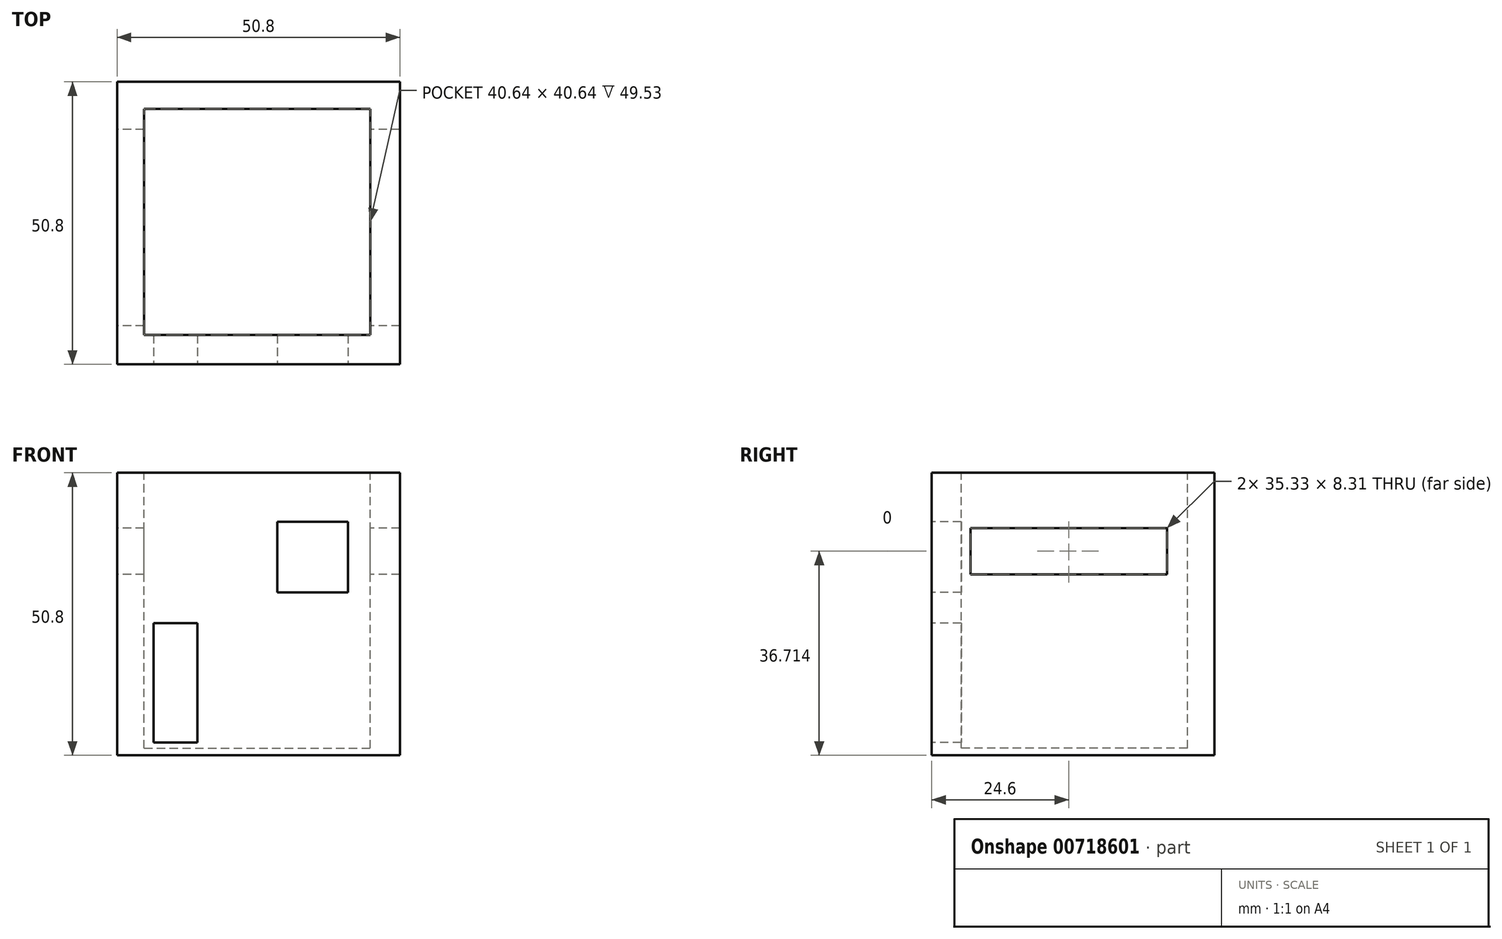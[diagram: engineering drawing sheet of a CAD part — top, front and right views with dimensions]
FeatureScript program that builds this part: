
annotation { "Feature Type Name" : "Feature", "Feature Type Description" : "" }
export const myFeature = defineFeature(function(context is Context, id is Id, definition is map)
    precondition{}
    {
        {
            var Q0;
            Q0=qCreatedBy(makeId("Top.planeOp"),FACE);
            var sketch = newSketch(context, id + "F0", { "sketchPlane" : qUnion([Q0])});
            skLineSegment(sketch, "E0.bottom", {"start": v(-23.32, 26.2) * mm, "end": v(27.48, 26.2) * mm});
            skLineSegment(sketch, "E0.top", {"start": v(-23.32, -24.6) * mm, "end": v(27.48, -24.6) * mm});
            skLineSegment(sketch, "E0.left", {"start": v(-23.32, 26.2) * mm, "end": v(-23.32, -24.6) * mm});
            skLineSegment(sketch, "E0.right", {"start": v(27.48, 26.2) * mm, "end": v(27.48, -24.6) * mm});
            skSolve(sketch);
        }
        {
            var Q0;
            Q0=makeQuery(id+"F0.imprint","IMPRINT",FACE,{"disambiguationData":[TD([[makeQuery(id+"F0.imprint","IMPRINT",EDGE,{"derivedFrom":sQuery(id+"F0.wireOp",EDGE,"E0.bottom")}),-1.0]])]});
            extrude(context, id + "F1", {"entities" : qUnion([Q0]), "depth" : 50.8 * mm, "offsetDistance" : 25.4 * mm});
        }
        {
            var Q0;
            Q0=makeQuery(id+"F1.opExtrude","CAP_FACE",FACE,{"disambiguationData":[OSD([sQuery(id+"F0.wireOp",EDGE,"E0.bottom"),sQuery(id+"F0.wireOp",EDGE,"E0.top"),sQuery(id+"F0.wireOp",EDGE,"E0.left"),sQuery(id+"F0.wireOp",EDGE,"E0.right")])],"isStart":false});
            var sketch = newSketch(context, id + "F2", { "sketchPlane" : qUnion([Q0])});
            skLineSegment(sketch, "E1.bottom", {"start": v(-18.47, 21.32) * mm, "end": v(22.17, 21.32) * mm});
            skLineSegment(sketch, "E1.top", {"start": v(-18.47, -19.32) * mm, "end": v(22.17, -19.32) * mm});
            skLineSegment(sketch, "E1.left", {"start": v(-18.47, 21.32) * mm, "end": v(-18.47, -19.32) * mm});
            skLineSegment(sketch, "E1.right", {"start": v(22.17, 21.32) * mm, "end": v(22.17, -19.32) * mm});
            skSolve(sketch);
        }
        {
            var Q0;
            Q0 = qSketchRegion(id + "F2", true);
            var Q1;
            Q1 = qConstructionFilter(qBodyType(qCreatedBy(id + "F2" ,EDGE), BodyType.WIRE), ConstructionObject.NO);
            extrude(context, id + "F3", {"entities" : qUnion([Q0]), "operationType" : NewBodyOperationType.REMOVE, "surfaceEntities" : qUnion([Q1]), "oppositeDirection" : true, "depth" : 49.53 * mm, "offsetDistance" : 25.4 * mm});
        }
        {
            var Q0;
            Q0=makeQuery(id+"F1.opExtrude","SWEPT_FACE",FACE,{"disambiguationData":[OSD([sQuery(id+"F0.wireOp",EDGE,"E0.top")])]});
            var sketch = newSketch(context, id + "F4", { "sketchPlane" : qUnion([Q0])});
            skLineSegment(sketch, "E2.bottom", {"start": v(-16.74, 23.78) * mm, "end": v(-8.9, 23.78) * mm});
            skLineSegment(sketch, "E2.top", {"start": v(-16.74, 2.3) * mm, "end": v(-8.9, 2.3) * mm});
            skLineSegment(sketch, "E2.left", {"start": v(-16.74, 23.78) * mm, "end": v(-16.74, 2.3) * mm});
            skLineSegment(sketch, "E2.right", {"start": v(-8.9, 23.78) * mm, "end": v(-8.9, 2.3) * mm});
            skSolve(sketch);
        }
        {
            var Q0;
            Q0 = qSketchRegion(id + "F4", true);
            extrude(context, id + "F5", {"entities" : qUnion([Q0]), "operationType" : NewBodyOperationType.REMOVE, "oppositeDirection" : true, "depth" : 25.4 * mm, "offsetDistance" : 25.4 * mm});
        }
        {
            var Q0;
            Q0=makeQuery(id+"F1.opExtrude","SWEPT_FACE",FACE,{"disambiguationData":[OSD([sQuery(id+"F0.wireOp",EDGE,"E0.top")])]});
            var sketch = newSketch(context, id + "F6", { "sketchPlane" : qUnion([Q0])});
            skLineSegment(sketch, "E3.bottom", {"start": v(5.46, 42) * mm, "end": v(18.16, 42) * mm});
            skLineSegment(sketch, "E3.top", {"start": v(5.46, 29.3) * mm, "end": v(18.16, 29.3) * mm});
            skLineSegment(sketch, "E3.left", {"start": v(5.46, 42) * mm, "end": v(5.46, 29.3) * mm});
            skLineSegment(sketch, "E3.right", {"start": v(18.16, 42) * mm, "end": v(18.16, 29.3) * mm});
            skSolve(sketch);
        }
        {
            var Q0;
            Q0 = qSketchRegion(id + "F6", true);
            extrude(context, id + "F7", {"entities" : qUnion([Q0]), "operationType" : NewBodyOperationType.REMOVE, "oppositeDirection" : true, "depth" : 7.62 * mm, "offsetDistance" : 25.4 * mm});
        }
        {
            var Q0;
            Q0=makeQuery(id+"F1.opExtrude","SWEPT_FACE",FACE,{"disambiguationData":[OSD([sQuery(id+"F0.wireOp",EDGE,"E0.left")])]});
            var sketch = newSketch(context, id + "F8", { "sketchPlane" : qUnion([Q0])});
            skLineSegment(sketch, "E4.bottom", {"start": v(-17.66, 32.56) * mm, "end": v(17.66, 32.56) * mm});
            skLineSegment(sketch, "E4.top", {"start": v(-17.66, 40.87) * mm, "end": v(17.66, 40.87) * mm});
            skLineSegment(sketch, "E4.left", {"start": v(-17.66, 32.56) * mm, "end": v(-17.66, 40.87) * mm});
            skLineSegment(sketch, "E4.right", {"start": v(17.66, 32.56) * mm, "end": v(17.66, 40.87) * mm});
            skSolve(sketch);
        }
        {
            var Q0;
            Q0 = qSketchRegion(id + "F8", true);
            extrude(context, id + "F9", {"entities" : qUnion([Q0]), "operationType" : NewBodyOperationType.REMOVE, "oppositeDirection" : true, "depth" : 50.8 * mm, "offsetDistance" : 25.4 * mm});
        }
    });
